# Revit family: Roof-Ventilator_VEDK_Direct-Drive_Carnes
name_source: partatom
category: Mechanical Equipment
revit_build: Autodesk Revit Architecture 2012 (Build: 20110916_2132(x64)
units: mm (PartAtom-declared; Revit-internal decimal feet)

## types (1)
- Roof-Ventilator_VEDK_Direct-Drive_Carnes
    04 CSI = 23 34 23
    95 CSI = 15830
    Assembly Code = D3040200
    Catalog URL = http://www.carnes.com
    Damper Size Sq. = 12"
    Default Elevation = 0"
    Description = Centrifugal Roof Exhausters
    E = 2 7/8"
    Housing = Aluminum-Carnes-Spun-Brushed
    Housing Radius = 12 7/8"
    IOM Instructions URL = http://www.carnes.com
    Inside Curb Cap = 15 1/2"
    Manufacturer = Carnes Company
    Manufacturer Fax = 608-845-6470
    Material = Spun Aluminum
    Model = VEDK
    Parts List URL = http://www.carnes.com
    Product Page URL = http://www.carnes.com
    Roof Curb O.D. Sq. = 14"
    Roof Opening Sq. = 13"
    Specifications URL = http://www.carnes.com
    Subcategory = Spun Aluminum Exhausters
    Tip Speed = 2.75 x RPM
    URL = http://www.carnes.com
    Unit Diameter = 25 3/4"
    Unit Height Extended = 23 7/8"
    Unit Height Standard = 13 3/8"
    Unit Weight (Less Motor) = 30 Lbs.
    Warranty URL = http://www.carnes.com
    ecoScorecard Product Page = http://ecoscorecard.com

## geometry (parser evidence)
native form markers: Blend x2, Sweep x3
no freeform markers — native parametric forms only
